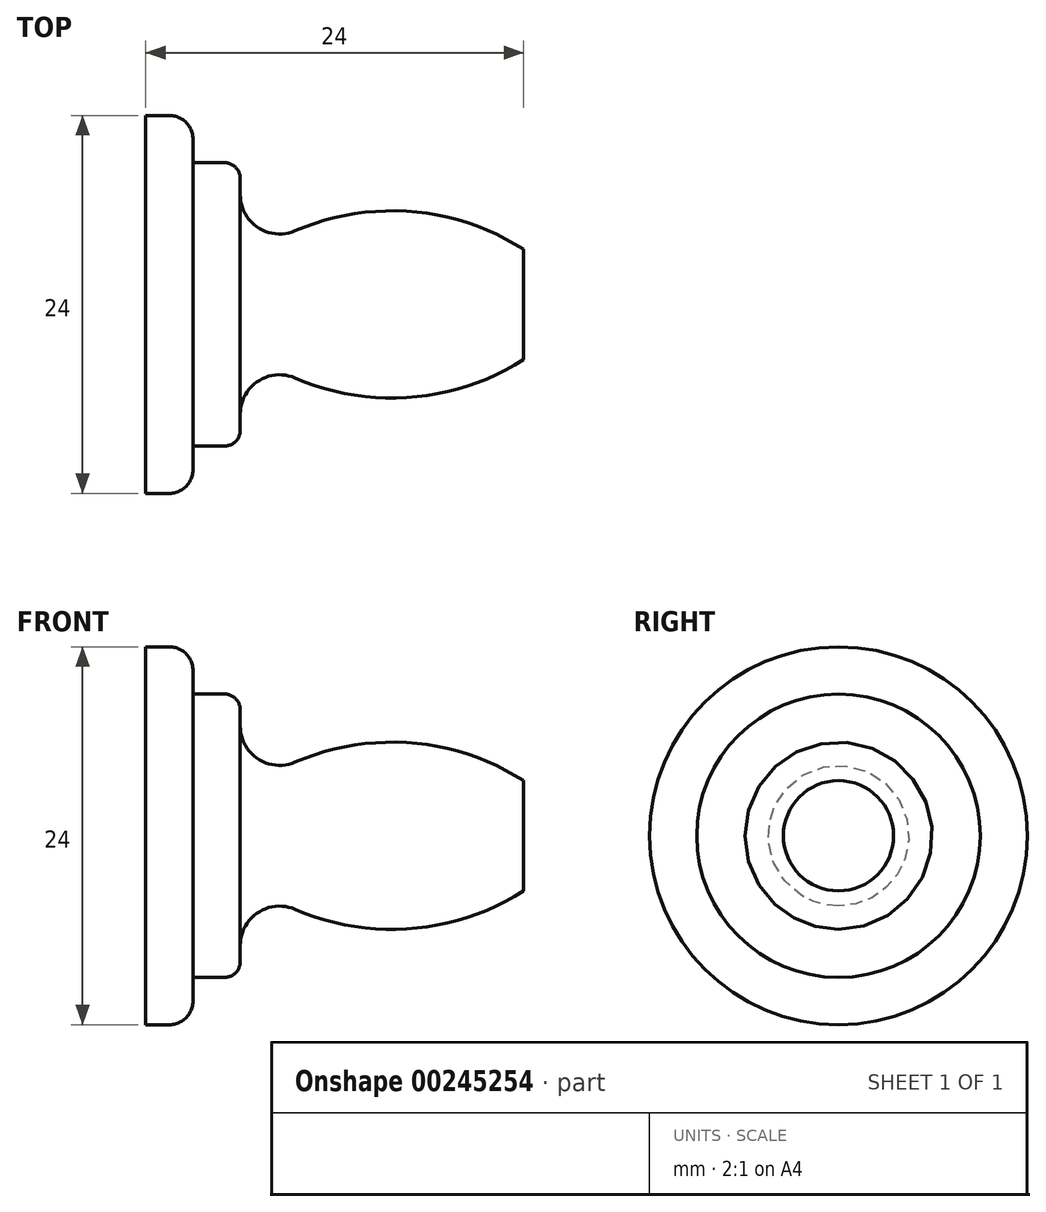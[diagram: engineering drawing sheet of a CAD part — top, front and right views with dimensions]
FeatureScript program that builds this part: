
annotation { "Feature Type Name" : "Feature", "Feature Type Description" : "" }
export const myFeature = defineFeature(function(context is Context, id is Id, definition is map)
    precondition{}
    {
        {
            var Q0;
            Q0=qCreatedBy(makeId("Front.planeOp"),FACE);
            var sketch = newSketch(context, id + "F0", { "sketchPlane" : qUnion([Q0])});
            skLineSegment(sketch, "E0", {"start": v(0, 0) * mm, "end": v(0, 3.5) * mm});
            skLineSegment(sketch, "E1", {"start": v(0, 0) * mm, "end": v(-24, 0) * mm});
            skLineSegment(sketch, "E2", {"start": v(-24, 0) * mm, "end": v(-24, 12) * mm});
            skLineSegment(sketch, "E3", {"start": v(-22.5, 12) * mm, "end": v(-24, 12) * mm});
            skLineSegment(sketch, "E4", {"start": v(-21, 10.5) * mm, "end": v(-21, 9) * mm});
            skLineSegment(sketch, "E5", {"start": v(-21, 9) * mm, "end": v(-19, 9) * mm});
            skLineSegment(sketch, "E6", {"start": v(-18, 8) * mm, "end": v(-18, 6.97) * mm});
            skPoint(sketch, "E7.end.orphan", {"position": v(-2.38, 12) * mm});
            skPoint(sketch, "E8.start.orphan", {"position": v(-9.53, 5) * mm});
            skArc(sketch, "E9", {"start": v(-18, 6.97) * mm, "mid": v(-16.87, 4.88) * mm, "end": v(-14.5, 4.67) * mm});
            skArc(sketch, "E10", {"start": v(0, 3.5) * mm, "mid": v(-7.1, 5.9) * mm, "end": v(-14.5, 4.67) * mm});
            skPoint(sketch, "E11.end.orphan", {"position": v(-1, 5) * mm});
            skPoint(sketch, "E12.orphan", {"position": v(0, 4) * mm});
            skPoint(sketch, "E13.visualSharp", {"position": v(-18, 9) * mm});
            skArc(sketch, "E13.filletArc", {"start": v(-18, 8) * mm, "mid": v(-18.3, 8.7) * mm, "end": v(-19, 9) * mm});
            skPoint(sketch, "E14.visualSharp", {"position": v(-21, 12) * mm});
            skArc(sketch, "E14.filletArc", {"start": v(-21, 10.5) * mm, "mid": v(-21.44, 11.56) * mm, "end": v(-22.5, 12) * mm});
            skSolve(sketch);
        }
        {
            var Q0;
            Q0=makeQuery(id+"F0.imprint","IMPRINT",FACE,{"disambiguationData":[TD([[makeQuery(id+"F0.imprint","IMPRINT",EDGE,{"derivedFrom":sQuery(id+"F0.wireOp",EDGE,"E0")}),1.0]])]});
            var Q1;
            Q1=sQuery(id+"F0.wireOp",EDGE,"E1");
            revolve(context, id + "F1", {"entities" : qUnion([Q0]), "axis" : qUnion([Q1]), "revolveType" : RevolveType.FULL});
        }
    });
